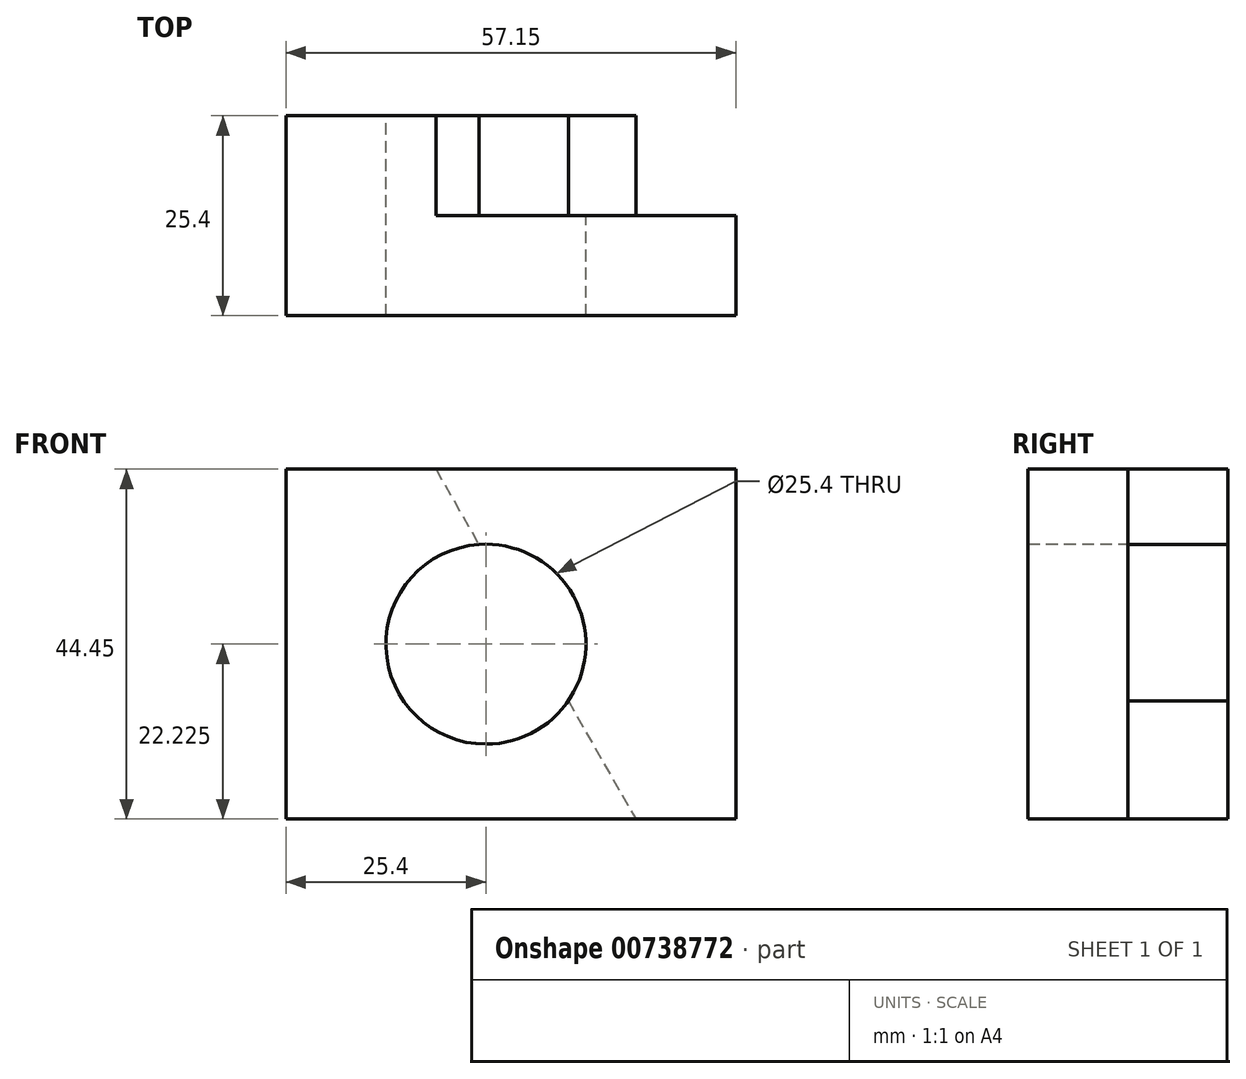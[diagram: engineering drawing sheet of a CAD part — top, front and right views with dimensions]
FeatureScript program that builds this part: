
annotation { "Feature Type Name" : "Feature", "Feature Type Description" : "" }
export const myFeature = defineFeature(function(context is Context, id is Id, definition is map)
    precondition{}
    {
        {
            var Q0;
            Q0=qCreatedBy(makeId("Front.planeOp"),FACE);
            var sketch = newSketch(context, id + "F0", { "sketchPlane" : qUnion([Q0])});
            skLineSegment(sketch, "E0", {"start": v(0, 0) * mm, "end": v(0, 44.45) * mm});
            skLineSegment(sketch, "E1", {"start": v(0, 44.45) * mm, "end": v(57.15, 44.45) * mm});
            skLineSegment(sketch, "E2", {"start": v(57.15, 44.45) * mm, "end": v(57.15, 0) * mm});
            skLineSegment(sketch, "E3", {"start": v(57.15, 0) * mm, "end": v(0, 0) * mm});
            skSolve(sketch);
        }
        {
            var Q0;
            Q0 = qSketchRegion(id + "F0", true);
            extrude(context, id + "F1", {"entities" : qUnion([Q0]), "depth" : 25.4 * mm, "offsetDistance" : 25.4 * mm});
        }
        {
            var Q0;
            Q0=qCreatedBy(makeId("Front.planeOp"),FACE);
            var sketch = newSketch(context, id + "F2", { "sketchPlane" : qUnion([Q0])});
            skLineSegment(sketch, "E4", {"start": v(0, 0) * mm, "end": v(0, 44.45) * mm});
            skLineSegment(sketch, "E5", {"start": v(0, 44.45) * mm, "end": v(19.05, 44.45) * mm});
            skLineSegment(sketch, "E6", {"start": v(19.05, 44.45) * mm, "end": v(44.45, 0) * mm});
            skLineSegment(sketch, "E7", {"start": v(44.45, 0) * mm, "end": v(0, 0) * mm});
            skLineSegment(sketch, "E8", {"start": v(44.45, 0) * mm, "end": v(57.15, 0) * mm});
            skLineSegment(sketch, "E9", {"start": v(57.15, 0) * mm, "end": v(57.15, 44.45) * mm});
            skLineSegment(sketch, "E10", {"start": v(57.15, 44.45) * mm, "end": v(19.05, 44.45) * mm});
            skSolve(sketch);
        }
        {
            var Q0;
            Q0=makeQuery(id+"F2.imprint","IMPRINT",FACE,{"disambiguationData":[TD([[makeQuery(id+"F2.imprint","IMPRINT",EDGE,{"derivedFrom":sQuery(id+"F2.wireOp",EDGE,"E6")}),1.0]])]});
            extrude(context, id + "F3", {"entities" : qUnion([Q0]), "operationType" : NewBodyOperationType.REMOVE, "depth" : 12.7 * mm, "offsetDistance" : 25.4 * mm});
        }
        {
            var Q0;
            Q0=qCreatedBy(makeId("Front.planeOp"),FACE);
            var sketch = newSketch(context, id + "F4", { "sketchPlane" : qUnion([Q0])});
            skLineSegment(sketch, "E11", {"start": v(25.4, 44.45) * mm, "end": v(25.4, 0) * mm});
            skCircle(sketch, "E12", {"center": v(25.4, 22.23) * mm, "radius": 12.7 * mm});
            skSolve(sketch);
        }
        {
            var Q0;
            Q0 = qSketchRegion(id + "F4", true);
            extrude(context, id + "F5", {"entities" : qUnion([Q0]), "operationType" : NewBodyOperationType.REMOVE, "endBound" : BoundingType.THROUGH_ALL, "depth" : 25.4 * mm, "offsetDistance" : 25.4 * mm});
        }
    });
